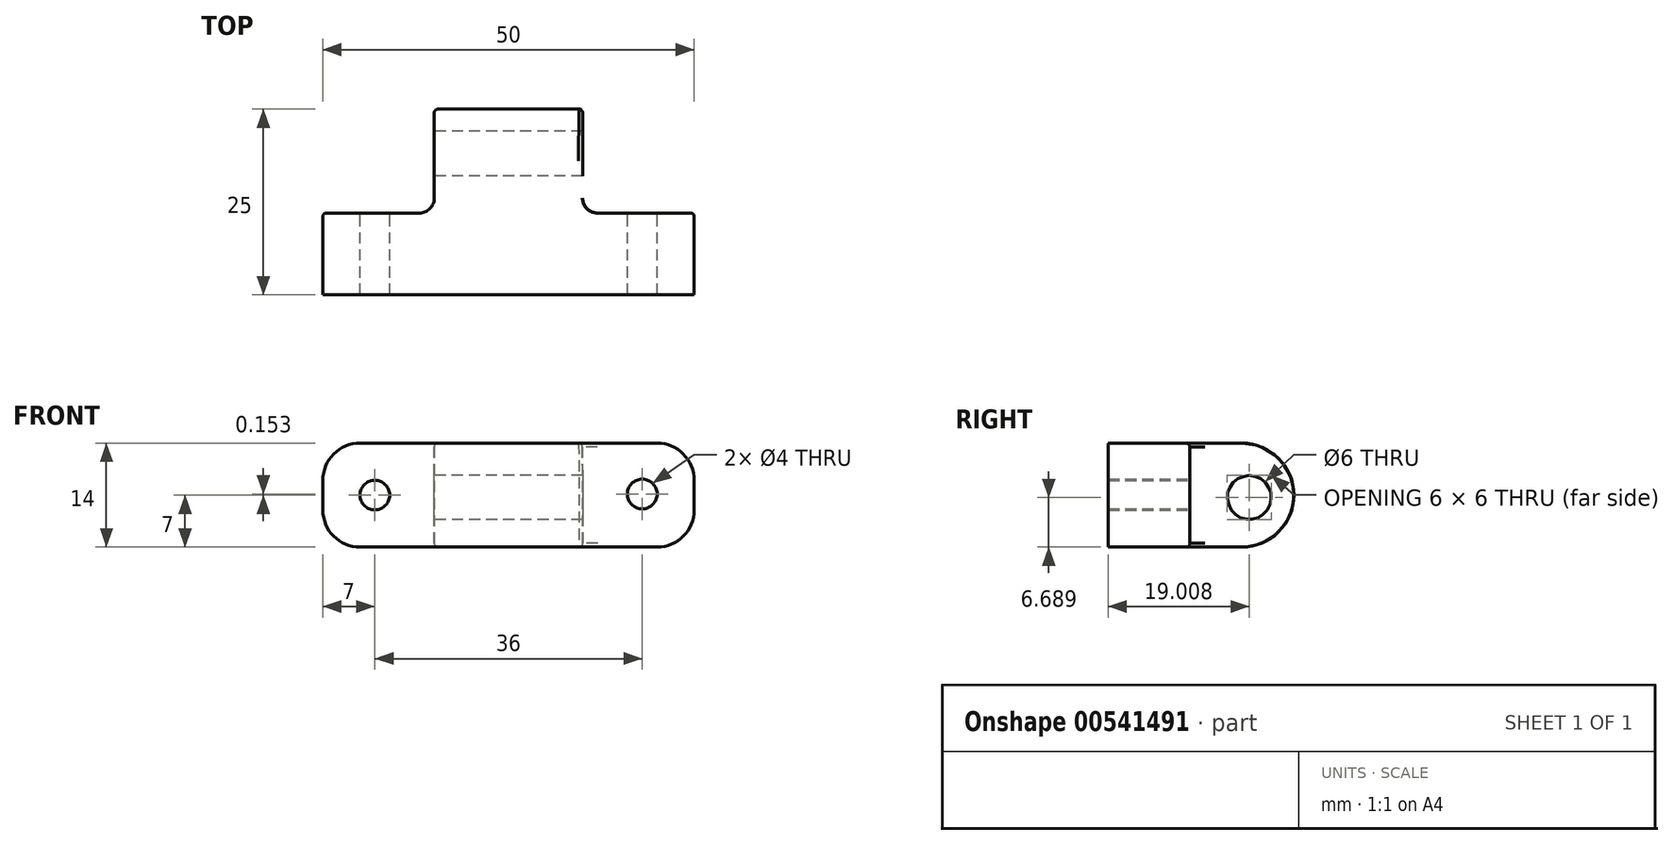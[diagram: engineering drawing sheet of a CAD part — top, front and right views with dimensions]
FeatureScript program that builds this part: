
annotation { "Feature Type Name" : "Feature", "Feature Type Description" : "" }
export const myFeature = defineFeature(function(context is Context, id is Id, definition is map)
    precondition{}
    {
        {
            var Q0;
            Q0=qCreatedBy(makeId("Front.planeOp"),FACE);
            var sketch = newSketch(context, id + "F0", { "sketchPlane" : qUnion([Q0])});
            skLineSegment(sketch, "E0.bottom", {"start": v(5, 0) * mm, "end": v(45, 0) * mm});
            skLineSegment(sketch, "E0.top", {"start": v(5, -14) * mm, "end": v(45, -14) * mm});
            skLineSegment(sketch, "E0.left", {"start": v(0, -5) * mm, "end": v(0, -9) * mm});
            skLineSegment(sketch, "E0.right", {"start": v(50, -5) * mm, "end": v(50, -9) * mm});
            skPoint(sketch, "E1.visualSharp", {"position": v(50, 0) * mm});
            skArc(sketch, "E1.filletArc", {"start": v(50, -5) * mm, "mid": v(48.54, -1.46) * mm, "end": v(45, 0) * mm});
            skPoint(sketch, "E2.visualSharp", {"position": v(50, -14) * mm});
            skArc(sketch, "E2.filletArc", {"start": v(45, -14) * mm, "mid": v(48.54, -12.54) * mm, "end": v(50, -9) * mm});
            skPoint(sketch, "E3.visualSharp", {"position": v(0, 0) * mm});
            skArc(sketch, "E3.filletArc", {"start": v(5, 0) * mm, "mid": v(1.46, -1.46) * mm, "end": v(0, -5) * mm});
            skPoint(sketch, "E4.visualSharp", {"position": v(0, -14) * mm});
            skArc(sketch, "E4.filletArc", {"start": v(0, -9) * mm, "mid": v(1.46, -12.54) * mm, "end": v(5, -14) * mm});
            skCircle(sketch, "E5", {"center": v(7, -7) * mm, "radius": 2 * mm});
            skPoint(sketch, "E5.centerSnap0", {"position": v(0, -7) * mm});
            skCircle(sketch, "E6", {"center": v(43, -6.85) * mm, "radius": 2 * mm});
            skLineSegment(sketch, "E7", {"start": v(35, 0) * mm, "end": v(35, -14) * mm, "construction": true});
            skLineSegment(sketch, "E8", {"start": v(15, 0) * mm, "end": v(15, -14) * mm, "construction": true});
            skSolve(sketch);
        }
        {
            var Q0;
            Q0=qCreatedBy(makeId("Front.planeOp"),FACE);
            var sketch = newSketch(context, id + "F1", { "sketchPlane" : qUnion([Q0])});
            skLineSegment(sketch, "E9", {"start": v(0, 0) * mm, "end": v(15, 0) * mm});
            skLineSegment(sketch, "E10", {"start": v(15, 0) * mm, "end": v(15, -14) * mm});
            skLineSegment(sketch, "E11", {"start": v(15, -14) * mm, "end": v(0, -14) * mm});
            skLineSegment(sketch, "E12", {"start": v(34.94, 0) * mm, "end": v(50, 0) * mm});
            skLineSegment(sketch, "E13", {"start": v(50, 0) * mm, "end": v(50, -14) * mm});
            skLineSegment(sketch, "E14", {"start": v(50, -14) * mm, "end": v(35, -14) * mm});
            skPoint(sketch, "E15.visualSharp", {"position": v(50, -14) * mm});
            skLineSegment(sketch, "E16", {"start": v(34.94, 0) * mm, "end": v(35, -14) * mm});
            skLineSegment(sketch, "E17", {"start": v(0, 0) * mm, "end": v(0, -14) * mm});
            skSolve(sketch);
        }
        {
            var Q0;
            Q0 = qSketchRegion(id + "F0", true);
            extrude(context, id + "F2", {"entities" : qUnion([Q0]), "depth" : 25 * mm, "offsetDistance" : 25 * mm});
        }
        {
            var Q0;
            Q0 = qSketchRegion(id + "F1", true);
            extrude(context, id + "F3", {"entities" : qUnion([Q0]), "operationType" : NewBodyOperationType.REMOVE, "depth" : 14 * mm, "offsetDistance" : 25 * mm});
        }
        {
            var Q0;
            Q0=qCreatedBy(makeId("Right.planeOp"),FACE);
            var sketch = newSketch(context, id + "F4", { "sketchPlane" : qUnion([Q0])});
            skCircle(sketch, "E18", {"center": v(-6, -7.31) * mm, "radius": 3 * mm});
            skSolve(sketch);
        }
        {
            var Q0;
            Q0 = qSketchRegion(id + "F4", true);
            extrude(context, id + "F5", {"entities" : qUnion([Q0]), "operationType" : NewBodyOperationType.REMOVE, "depth" : 74.4 * mm, "offsetDistance" : 25 * mm});
        }
        {
            var Q0;
            Q0=makeQuery(id+"F2.opExtrude","CAP_EDGE",EDGE,{"disambiguationData":[OSD([sQuery(id+"F0.wireOp",EDGE,"E0.bottom")])],"isStart":true});
            var Q1;
            Q1=makeQuery(id+"F2.opExtrude","CAP_EDGE",EDGE,{"disambiguationData":[OSD([sQuery(id+"F0.wireOp",EDGE,"E0.top")])],"isStart":true});
            fillet(context, id + "F6", {"entities" : qUnion([Q0, Q1]), "radius" : 7 * mm, "tangentPropagation" : true, "allowEdgeOverflow" : false});
        }
        {
            var Q0;
            Q0=makeQuery(id+"F3.boolean.opBoolean","COPY",EDGE,{"derivedFrom":makeQuery(id+"F3.opExtrude","CAP_EDGE",EDGE,{"disambiguationData":[OSD([sQuery(id+"F1.wireOp",EDGE,"E10")])],"isStart":false})});
            fillet(context, id + "F7", {"entities" : qUnion([Q0]), "radius" : 2 * mm, "tangentPropagation" : true, "allowEdgeOverflow" : false});
        }
        {
            var Q0;
            Q0=makeQuery(id+"F3.boolean.opBoolean","COPY",EDGE,{"derivedFrom":makeQuery(id+"F3.opExtrude","CAP_EDGE",EDGE,{"disambiguationData":[OSD([sQuery(id+"F1.wireOp",EDGE,"E16")])],"isStart":false})});
            fillet(context, id + "F8", {"entities" : qUnion([Q0]), "radius" : 2 * mm, "tangentPropagation" : true, "allowEdgeOverflow" : false});
        }
        {
            var Q0;
            Q0=makeQuery(id+"F3.boolean.opBoolean","INTERSECT",EDGE,{"derivedFrom":[makeQuery(id+"F2.opExtrude","SWEPT_FACE",FACE,{"disambiguationData":[OSD([sQuery(id+"F0.wireOp",EDGE,"E4.filletArc")])]}),makeQuery(id+"F3.opExtrude","CAP_FACE",FACE,{"disambiguationData":[OSD([sQuery(id+"F1.wireOp",EDGE,"E9"),sQuery(id+"F1.wireOp",EDGE,"E10"),sQuery(id+"F1.wireOp",EDGE,"E11"),sQuery(id+"F1.wireOp",EDGE,"E17")])],"isStart":false})]});
            var Q1;
            Q1=makeQuery(id+"F3.boolean.opBoolean","COPY",EDGE,{"derivedFrom":makeQuery(id+"F3.opExtrude","CAP_EDGE",EDGE,{"disambiguationData":[OSD([sQuery(id+"F1.wireOp",EDGE,"E11")])],"isStart":false})});
            fillet(context, id + "F9", {"entities" : qUnion([Q0, Q1]), "radius" : .5 * mm, "tangentPropagation" : true, "allowEdgeOverflow" : false});
        }
        {
            var Q0;
            Q0=makeQuery(id+"F3.boolean.opBoolean","INTERSECT",EDGE,{"derivedFrom":[makeQuery(id+"F2.opExtrude","SWEPT_FACE",FACE,{"disambiguationData":[OSD([sQuery(id+"F0.wireOp",EDGE,"E1.filletArc")])]}),makeQuery(id+"F3.opExtrude","CAP_FACE",FACE,{"disambiguationData":[OSD([sQuery(id+"F1.wireOp",EDGE,"E12"),sQuery(id+"F1.wireOp",EDGE,"E13"),sQuery(id+"F1.wireOp",EDGE,"E14"),sQuery(id+"F1.wireOp",EDGE,"E16")])],"isStart":false})]});
            var Q1;
            Q1=makeQuery(id+"F3.boolean.opBoolean","COPY",EDGE,{"derivedFrom":makeQuery(id+"F3.opExtrude","CAP_EDGE",EDGE,{"disambiguationData":[OSD([sQuery(id+"F1.wireOp",EDGE,"E12")])],"isStart":false})});
            fillet(context, id + "F10", {"entities" : qUnion([Q0, Q1]), "radius" : .5 * mm, "tangentPropagation" : true, "allowEdgeOverflow" : false});
        }
    });
